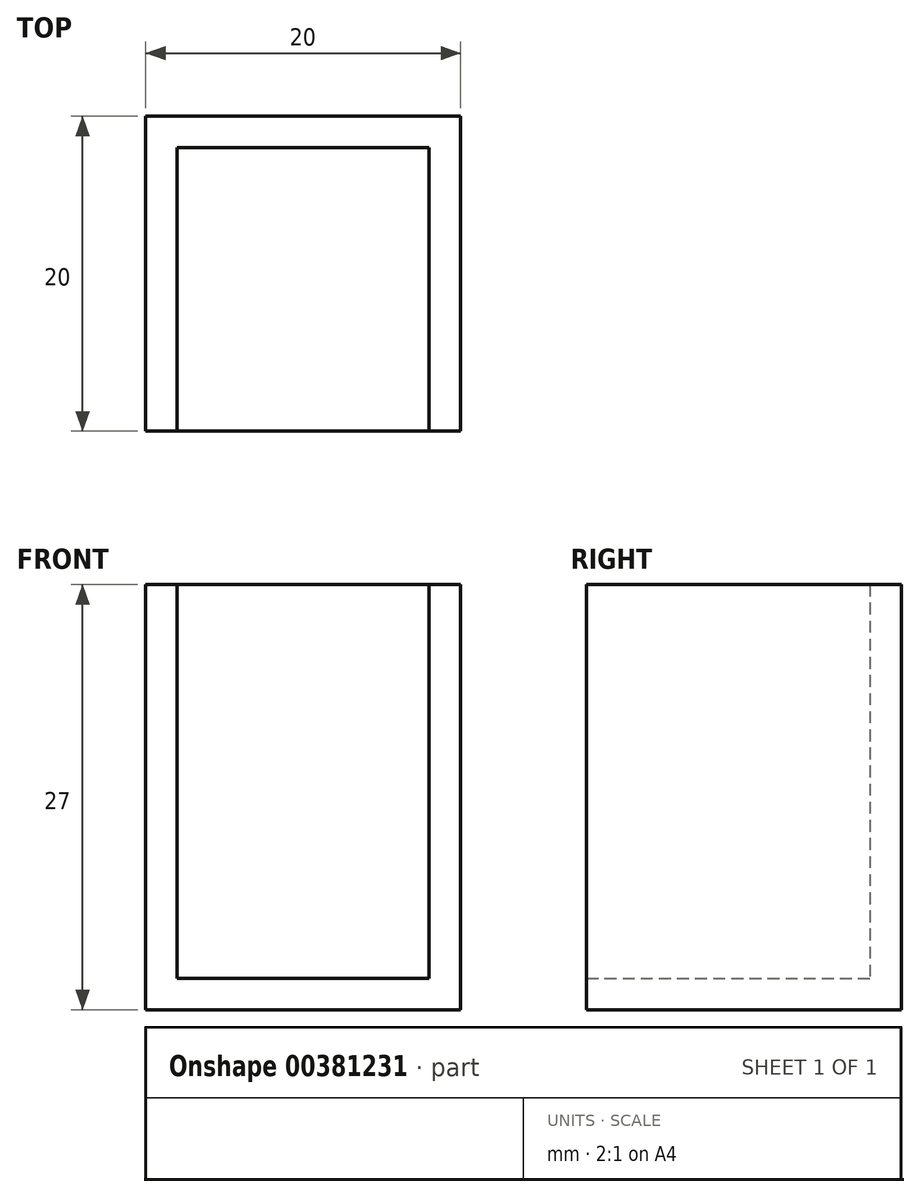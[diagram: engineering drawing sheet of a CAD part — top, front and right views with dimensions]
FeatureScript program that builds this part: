
annotation { "Feature Type Name" : "Feature", "Feature Type Description" : "" }
export const myFeature = defineFeature(function(context is Context, id is Id, definition is map)
    precondition{}
    {
        {
            var Q0;
            Q0=qCreatedBy(makeId("Top.planeOp"),FACE);
            var sketch = newSketch(context, id + "F0", { "sketchPlane" : qUnion([Q0])});
            skLineSegment(sketch, "E0.bottom", {"start": v(-10, 10) * mm, "end": v(10, 10) * mm});
            skLineSegment(sketch, "E0.top", {"start": v(-10, -10) * mm, "end": v(10, -10) * mm});
            skLineSegment(sketch, "E0.left", {"start": v(-10, 10) * mm, "end": v(-10, -10) * mm});
            skLineSegment(sketch, "E0.right", {"start": v(10, 10) * mm, "end": v(10, -10) * mm});
            skPoint(sketch, "E0.middle", {"position": v(0, 0) * mm});
            skPoint(sketch, "E1", {"position": v(-8, -10) * mm});
            skPoint(sketch, "E2", {"position": v(8, -10) * mm});
            skLineSegment(sketch, "E3", {"start": v(8, -10) * mm, "end": v(8, 8) * mm});
            skLineSegment(sketch, "E4", {"start": v(8, 8) * mm, "end": v(-8, 8) * mm});
            skLineSegment(sketch, "E5", {"start": v(-8, 8) * mm, "end": v(-8, -10) * mm});
            skSolve(sketch);
        }
        {
            var Q0;
            Q0=makeQuery(id+"F0.imprint","IMPRINT",FACE,{"disambiguationData":[TD([[makeQuery(id+"F0.imprint","IMPRINT",EDGE,{"derivedFrom":sQuery(id+"F0.wireOp",EDGE,"E0.bottom")}),-1.0]])]});
            extrude(context, id + "F1", {"entities" : qUnion([Q0]), "depth" : 25 * mm});
        }
        {
            var Q0;
            Q0 = qSketchRegion(id + "F0", true);
            extrude(context, id + "F2", {"entities" : qUnion([Q0]), "operationType" : NewBodyOperationType.ADD, "oppositeDirection" : true, "depth" : 2 * mm});
        }
    });
